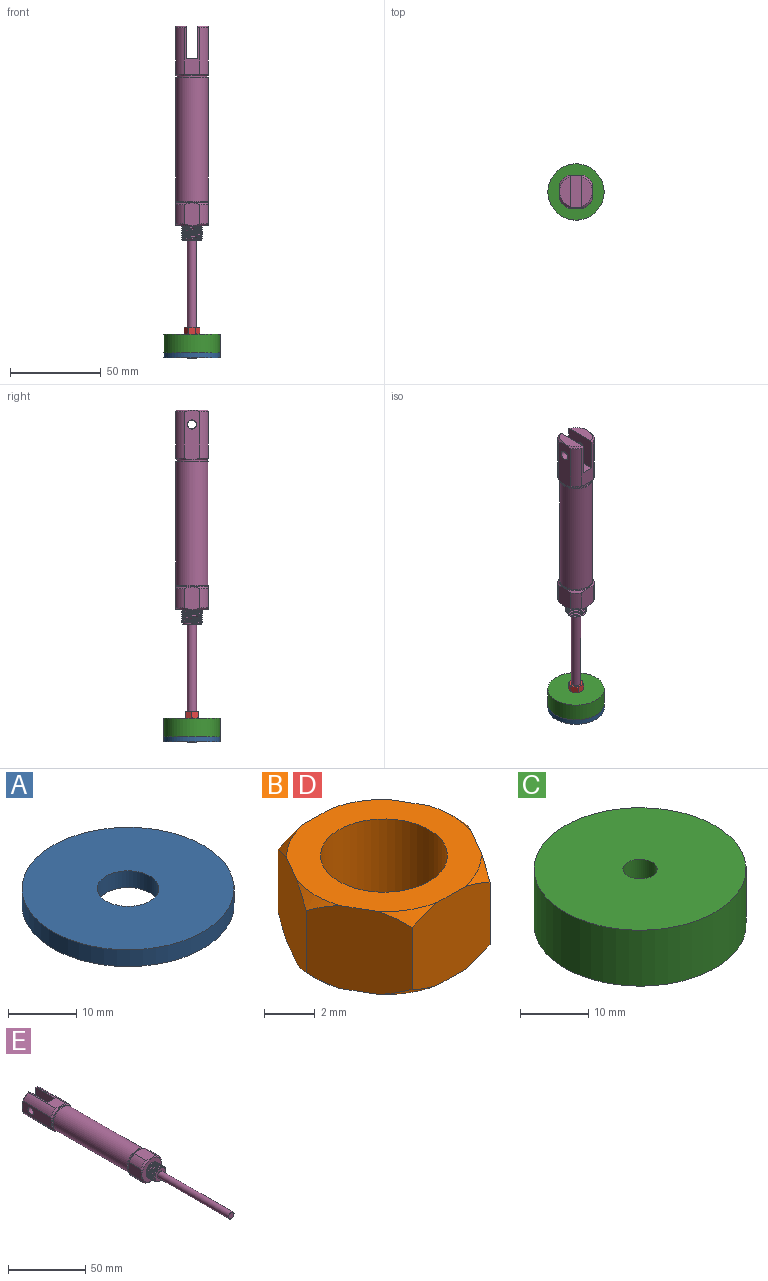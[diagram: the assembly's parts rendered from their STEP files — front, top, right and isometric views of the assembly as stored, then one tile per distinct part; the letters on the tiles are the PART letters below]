
ASSEMBLY  parts=5 mates=4
PART A: 4 faces, bbox 31x31x3 mm
  f0: cylinder r=4.5mm len=9mm, axis (0,0,-1), area 84.8mm2, adj f2,f3
  f1: cylinder r=15.5mm len=31mm, axis (0,0,-1), area 292.2mm2, adj f2,f3
  f2: plane 31x31mm, normal (0,0,1), area 691.2mm2, adj f0,f1
  f3: plane 31x31mm, normal (0,0,-1), area 691.2mm2, adj f0,f1
PART B: 21 faces, bbox 8.8x8.7x4.2 mm
  f0: plane 4.18x3.92mm, normal (0.86,-0.5,0), area 16.1mm2, adj f1,f5,f6,f8,f10,f12,f19,f20
  f1: plane 4.18x3.93mm, normal (0.87,0.5,0), area 16.1mm2, adj f0,f2,f6,f8,f17,f18,f19,f20
  f2: plane 4.5x4.18mm, normal (0,1,0), area 16.1mm2, adj f1,f3,f6,f8,f15,f16,f17,f18
  f3: plane 4.18x3.92mm, normal (-0.86,0.5,0), area 16.1mm2, adj f2,f4,f6,f8,f13,f14,f15,f16
  f4: plane 4.18x3.93mm, normal (-0.87,-0.5,0), area 16.1mm2, adj f3,f5,f6,f8,f9,f11,f13,f14
  f5: plane 4.5x4.18mm, normal (0,-1,0), area 16.1mm2, adj f0,f4,f6,f8,f9,f10,f11,f12
  f6: plane 7.66x7.51mm, normal (0,0,1), area 26mm2, adj f0,f1,f2,f3,f4,f5,f7,f11
  f7: cylinder r=2.5mm len=5mm, axis (0,0,-1), area 62.8mm2, adj f6,f8
  f8: plane 7.66x7.51mm, normal (0,0,-1), area 26mm2, adj f0,f1,f2,f3,f4,f5,f7,f9
  f9: cone r=3.83mm half-angle=45deg, axis (0,0,1), area 0.9mm2, adj f4,f5,f8
  f10: cone r=3.83mm half-angle=45deg, axis (0,0,1), area 0.9mm2, adj f0,f5,f8
  f11: cone r=3.83mm half-angle=45deg, axis (0,0,-1), area 0.9mm2, adj f4,f5,f6
  f12: cone r=3.83mm half-angle=45deg, axis (0,0,-1), area 0.9mm2, adj f0,f5,f6
  f13: cone r=3.83mm half-angle=45deg, axis (0,0,1), area 0.9mm2, adj f3,f4,f8
  f14: cone r=3.83mm half-angle=45deg, axis (0,0,-1), area 0.9mm2, adj f3,f4,f6
  f15: cone r=3.83mm half-angle=45deg, axis (0,0,1), area 0.9mm2, adj f2,f3,f8
  f16: cone r=3.83mm half-angle=45deg, axis (0,0,-1), area 0.9mm2, adj f2,f3,f6
  f17: cone r=3.83mm half-angle=45deg, axis (0,0,1), area 0.9mm2, adj f1,f2,f8
  f18: cone r=3.83mm half-angle=45deg, axis (0,0,-1), area 0.9mm2, adj f1,f2,f6
  f19: cone r=3.83mm half-angle=45deg, axis (0,0,1), area 0.9mm2, adj f0,f1,f8
  f20: cone r=3.83mm half-angle=45deg, axis (0,0,-1), area 0.9mm2, adj f0,f1,f6
PART C: 6 faces, bbox 31x31x10 mm
  f0: cylinder r=2.5mm len=8mm, axis (0,0,-1), area 125.7mm2, adj f2,f5
  f1: cylinder r=15.5mm len=31mm, axis (0,0,-1), area 973.9mm2, adj f2,f3
  f2: plane 31x31mm, normal (0,0,1), area 735.1mm2, adj f0,f1
  f3: plane 31x31mm, normal (0,0,-1), area 691.2mm2, adj f1,f4
  f4: cylinder r=4.5mm len=9mm, axis (0,0,-1), area 56.5mm2, adj f3,f5
  f5: plane 9x9mm, normal (0,0,-1), area 44mm2, adj f0,f4
PART D: same geometry as B
PART E: 59 faces, bbox 21x184x21 mm
  f0: plane 16x6.13mm, normal (0,-1,0), area 10.1mm2, adj f6,f41,f42,f57,f58
  f1: plane 18.47x18.47mm, normal (0,-1,0), area 166.8mm2, adj f2,f21,f22,f23,f24,f52,f53
  f2: cylinder r=5mm len=10mm, axis (0,1,0), area 33.9mm2, adj f1,f26,f51,f52,f53
  f3: cylinder r=9mm len=68mm, axis (0,1,0), area 3845.3mm2, adj f5,f7
  f4: cylinder r=8.5mm len=17mm, axis (0,-1,0), area 53.4mm2, adj f5,f16
  f5: plane 18x18mm, normal (0,-1,0), area 27.5mm2, adj f3,f4
  f6: cylinder r=8.5mm len=17mm, axis (0,1,0), area 54.9mm2, adj f0,f7,f28,f57,f58
  f7: plane 18x18mm, normal (0,1,0), area 27.5mm2, adj f3,f6
  f8: plane 13.22x9.44mm, normal (-1,0,0), area 103mm2, adj f9,f15,f19,f20,f21,f24
  f9: cylinder r=10mm len=10.5mm, axis (0,1,0), area 70.2mm2, adj f8,f10,f20,f21
  f10: plane 13.22x9.44mm, normal (0,0,-1), area 103mm2, adj f9,f11,f18,f20,f21,f22
  f11: cylinder r=10mm len=10.5mm, axis (0,1,0), area 70.2mm2, adj f10,f12,f18,f22
  f12: plane 13.22x9.44mm, normal (1,0,0), area 103mm2, adj f11,f13,f17,f18,f22,f23
  f13: cylinder r=10mm len=10.5mm, axis (0,1,0), area 70.2mm2, adj f12,f14,f17,f23
  f14: plane 13.22x9.44mm, normal (0,0,1), area 103mm2, adj f13,f15,f17,f19,f23,f24
  f15: cylinder r=10mm len=10.5mm, axis (0,1,0), area 70.2mm2, adj f8,f14,f19,f24
  f16: plane 18x18mm, normal (0,1,0), area 27.5mm2, adj f4,f17,f18,f19,f20
  f17: cone r=10mm half-angle=45deg, axis (0,-1,0), area 14.9mm2, adj f12,f13,f14,f16
  f18: cone r=10mm half-angle=45deg, axis (0,-1,0), area 14.9mm2, adj f10,f11,f12,f16
  f19: cone r=10mm half-angle=45deg, axis (0,-1,0), area 14.9mm2, adj f8,f14,f15,f16
  f20: cone r=10mm half-angle=45deg, axis (0,-1,0), area 14.9mm2, adj f8,f9,f10,f16
  f21: cone r=9mm half-angle=45deg, axis (0,1,0), area 14.9mm2, adj f1,f8,f9,f10
  f22: cone r=9mm half-angle=45deg, axis (0,1,0), area 14.9mm2, adj f1,f10,f11,f12
  f23: cone r=9mm half-angle=45deg, axis (0,1,0), area 14.9mm2, adj f1,f12,f13,f14
  f24: cone r=9mm half-angle=45deg, axis (0,1,0), area 14.9mm2, adj f1,f8,f14,f15
  f25: cylinder r=2.6mm len=8mm, axis (0,1,0), area 130.7mm2, adj f26,f27
  f26: plane 10x10mm, normal (0,-1,0), area 57.3mm2, adj f2,f25
  f27: plane 5.2x5.2mm, normal (0,-1,0), area 1.6mm2, adj f25,f54
  f28: plane 16x6.13mm, normal (0,-1,0), area 10.1mm2, adj f6,f43,f44,f57,f58
  f29: plane 28.22x9.44mm, normal (1,0,0), area 214.2mm2, adj f30,f34,f43,f44,f45,f48,f50
  f30: cylinder r=10mm len=25.5mm, axis (0,-1,0), area 170.5mm2, adj f29,f31,f44,f45
  f31: plane 25.98x8.76mm, normal (0,0,-1), area 112.3mm2, adj f30,f32,f36,f37,f45,f46,f56,f58
  f32: plane 18.01x18.01mm, normal (-1,0,0), area 304mm2, adj f31,f33,f35,f45,f48,f50,f56
  f33: plane 25.98x8.76mm, normal (0,0,1), area 112.3mm2, adj f32,f34,f36,f39,f47,f48,f56,f57
  f34: cylinder r=10mm len=25.5mm, axis (0,-1,0), area 170.5mm2, adj f29,f33,f43,f48
  f35: plane 16.79x5.75mm, normal (0,1,0), area 70mm2, adj f32,f45,f48
  f36: plane 18.01x18.01mm, normal (1,0,0), area 304mm2, adj f31,f33,f40,f46,f47,f49,f56
  f37: cylinder r=10mm len=25.5mm, axis (0,-1,0), area 170.5mm2, adj f31,f38,f42,f46
  f38: plane 28.22x9.44mm, normal (-1,0,0), area 214.2mm2, adj f37,f39,f41,f42,f46,f47,f49
  f39: cylinder r=10mm len=25.5mm, axis (0,-1,0), area 170.5mm2, adj f33,f38,f41,f47
  f40: plane 16.79x5.75mm, normal (0,1,0), area 70mm2, adj f36,f46,f47
  f41: cone r=10mm half-angle=45deg, axis (0,1,0), area 11.8mm2, adj f0,f38,f39,f57
  f42: cone r=10mm half-angle=45deg, axis (0,1,0), area 11.8mm2, adj f0,f37,f38,f58
  f43: cone r=10mm half-angle=45deg, axis (0,1,0), area 11.8mm2, adj f28,f29,f34,f57
  f44: cone r=10mm half-angle=45deg, axis (0,1,0), area 11.8mm2, adj f28,f29,f30,f58
  f45: cone r=9mm half-angle=45deg, axis (0,-1,0), area 13mm2, adj f29,f30,f31,f32,f35
  f46: cone r=9mm half-angle=45deg, axis (0,-1,0), area 13mm2, adj f31,f36,f37,f38,f40
  f47: cone r=9mm half-angle=45deg, axis (0,-1,0), area 13mm2, adj f33,f36,f38,f39,f40
  f48: cone r=9mm half-angle=45deg, axis (0,-1,0), area 13mm2, adj f29,f32,f33,f34,f35
  f49: cylinder r=2.5mm len=5.75mm, axis (-1,0,0), area 90.3mm2, adj f36,f38
  f50: cylinder r=2.5mm len=5.75mm, axis (-1,0,0), area 90.3mm2, adj f29,f32
  f51: plane 0.8x0.69mm, normal (0,0,-1), area 0.3mm2, adj f2,f52,f53
  f52: bspline ~13.15x11.39mm, area 198.8mm2, adj f1,f2,f51,f53
  f53: bspline ~13.15x11.39mm, area 210.3mm2, adj f1,f2,f51,f52
  f54: cylinder r=2.5mm len=73mm, axis (0,1,0), area 1146.7mm2, adj f27,f55
  f55: plane 5x5mm, normal (0,-1,0), area 19.6mm2, adj f54
  f56: plane 18x6.5mm, normal (0,1,0), area 117mm2, adj f31,f32,f33,f36
  f57: plane 8.97x1.25mm, normal (0,-0.71,0.71), area 9.3mm2, adj f0,f6,f28,f33,f41,f43
  f58: plane 9.72x2mm, normal (0,-0.71,-0.71), area 9.3mm2, adj f0,f6,f28,f31,f42,f44
PLACE A rot(axis=(1,0,0),0deg) t=(-85.96,100.65,-241.49)mm
PLACE B rot(axis=(1,0,0),0deg) t=(-51.43,54.8,-240.49)mm
PLACE C rot(axis=(1,0,0),0deg) t=(-51.43,54.8,-238.49)mm
PLACE D rot(axis=(1,0,0),0deg) t=(-51.43,54.8,-228.49)mm
PLACE E rot(axis=(1,0,0),90deg) t=(-51.43,54.8,-120.99)mm
MATE fastened B.f7 <-> C.f4  axis (0,0,-1) through (-51.43,54.8,-236.49)mm
MATE fastened C.f0 <-> D.f7  axis (0,0,1) through (-51.43,54.8,-228.49)mm
MATE fastened A.f0 <-> C.f1  axis (0,0,1) through (-51.43,54.8,-238.49)mm
MATE fastened E.f54 <-> D.f9  axis (0,0,-1) through (-51.43,54.8,-241.49)mm
